# Revit family: Terminal_Unit-Carnes-AVCD-Single_Duct-Circular
name_source: partatom
category: Mechanical Equipment
revit_build: Autodesk Revit MEP 2012 (Build: 20110309_2315(x64)
units: mm (PartAtom-declared; Revit-internal decimal feet)

## types (8) — shared parameters
04 CSI = 23 34 23
95 CSI = 15830
Airflow = 0.0 L/s
Amperage = 0 A
Apparent Load = 0 VA
Assembly Code = D3040200
Catalog URL = http://www.carnes.com
Default Elevation = 0"
Description = Single Duct Terminal Units
Frequency = 0 Hz
IOM Instructions URL = http://www.carnes.com
Manufacturer = CARNES COMPANY
Manufacturer Fax = 608-845-6470
Material = Galvanized Steel
Modeling Numbering System = http://www.carnes.com
Number of Poles = 1
Phase = 1
Product Page URL = http://www.carnes.com
Spec Sheet URL = http://www.carnes.com
Subcategory = Air Volume Terminal Units
URL = http://www.carnes.com
Unit = Metal - Carnes - Steel
Voltage = 0 V
Wattage = 0 W
ecoScorecard Product Page = http://ecoscorecard.com
zero-valued in all types: Power Factor

## per-type parameters (varying)
| type | A | B | C | E | Electronic Min. CFM Range | F | Inlet Diameter | Inlet Height | Inlet Radius | Inlet Width | Max CFM Range | Pneu. Min. CFM Range | Rated CFM |
| AVCD 05 | 12" | 8" | 20 1/2" | 17" | ø or 45-140 | 7 5/8" | 5 | 5" | 2 1/2" | 5" | 210 - 350 | ø or 75 - 140 | 350 m³ |
| AVCD 06 | 12" | 8" | 20 1/2" | 17" | ø or 65 - 200 | 7 5/8" | 6 | 5" | 3" | 6" | 300 - 500 | ø or 110 - 200 | 500 m³ |
| AVCD 07 | 12" | 10" | 20 1/2" | 17" | ø or 85 - 280 | 10 1/8" | 7 | 7" | 3 1/2" | 7" | 420 - 700 | ø or 140 - 280 | 700 m³ |
| AVCD 08 | 12" | 10" | 20 1/2" | 17" | ø or 105 - 400 | 10 1/8" | 8 | 8" | 4" | 8" | 600 - 1000 | ø or 185 - 400 | 1000 m³ |
| AVCD 10 | 14" | 12 1/2" | 20 1/2" | 19" | ø or 155 - 600 | 12 5/8" | 10 | 10" | 5" | 10" | 900 - 1500 | ø or 300 - 600 | 1500 m³ |
| AVCD 12 | 16" | 15" | 20 1/2" | 21" | ø or 225 - 920 | 15 1/8" | 12 | 12" | 6" | 12" | 1380 - 2300 | ø or 430 - 920 | 2300 m³ |
| AVCD 14 | 20" | 17 1/2" | 20 1/2" | 25" | ø or 335 - 1240 | 17 5/8" | 14 | 14" | 7" | 14" | 1860 - 3100 | ø or 600 - 1240 | 3100 m³ |
| AVCD 16 | 24" | 18" | 21 1/2" | 29" | ø or 465 - 1680 | 17 5/8" | 16 | 16" | 8" | 16" | 2520 - 4200 | ø or 1100 - 2200 | 4200 m³ |

note: column(s) folded — value = type name in every type: Model

## geometry (parser evidence)
native form markers: Blend x2, Sweep x14
no freeform markers — native parametric forms only
